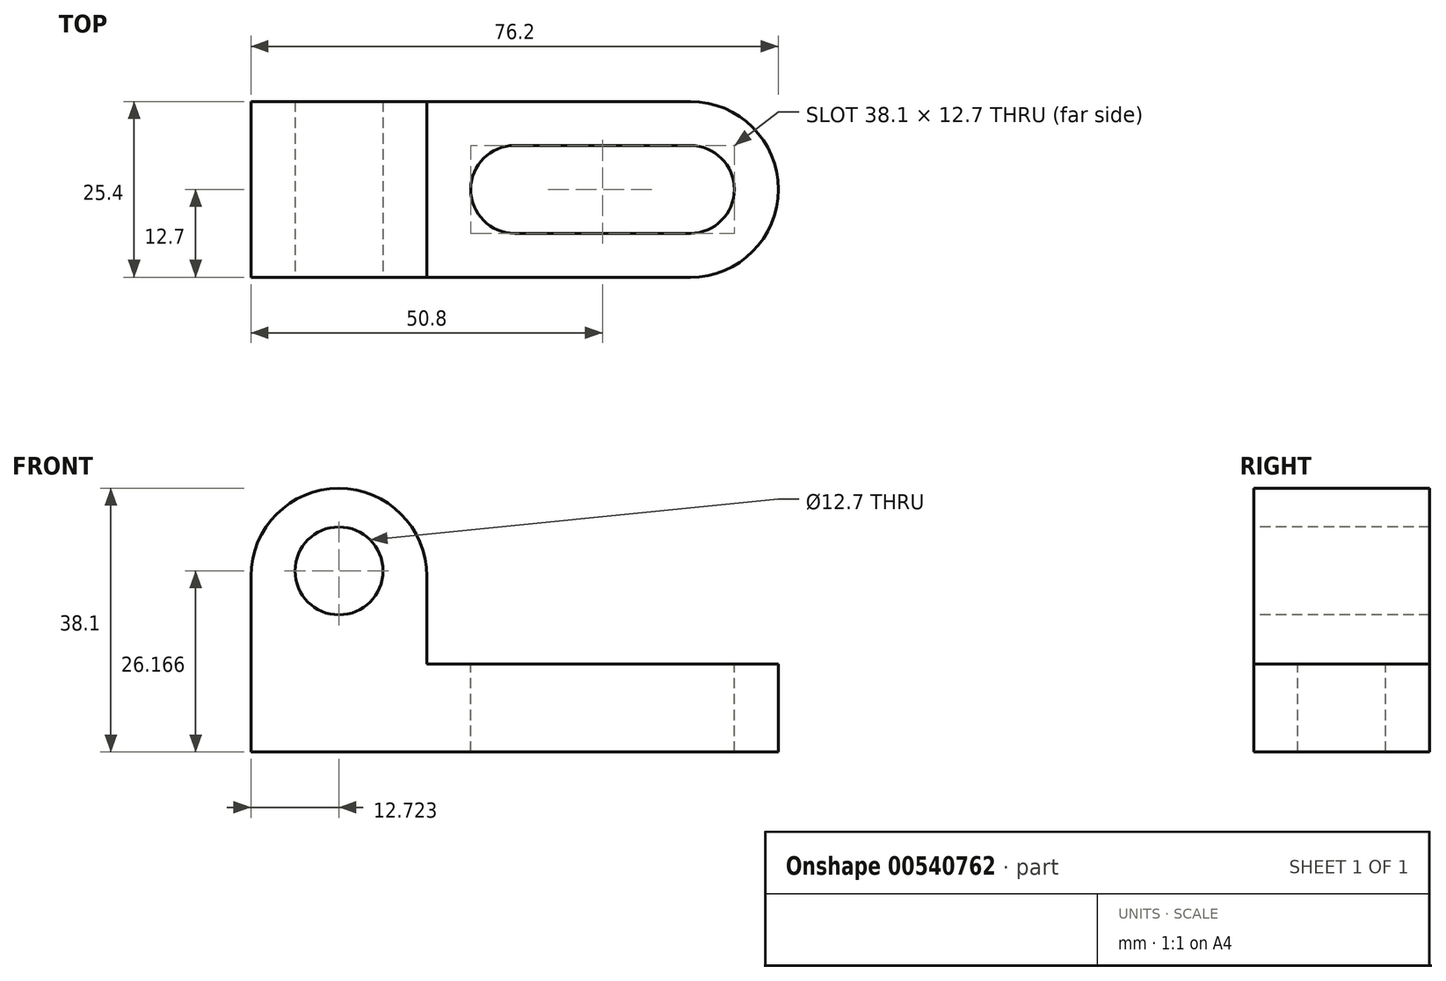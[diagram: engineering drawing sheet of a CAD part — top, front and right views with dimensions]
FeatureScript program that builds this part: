
annotation { "Feature Type Name" : "Feature", "Feature Type Description" : "" }
export const myFeature = defineFeature(function(context is Context, id is Id, definition is map)
    precondition{}
    {
        {
            var Q0;
            Q0=qCreatedBy(makeId("Front.planeOp"),FACE);
            var sketch = newSketch(context, id + "F0", { "sketchPlane" : qUnion([Q0])});
            skLineSegment(sketch, "E0", {"start": v(0, 0) * mm, "end": v(76.2, 0) * mm});
            skLineSegment(sketch, "E1", {"start": v(76.2, 0) * mm, "end": v(76.2, 12.7) * mm});
            skLineSegment(sketch, "E2", {"start": v(76.2, 12.7) * mm, "end": v(25.4, 12.7) * mm});
            skLineSegment(sketch, "E3", {"start": v(25.4, 12.7) * mm, "end": v(25.4, 38.1) * mm});
            skLineSegment(sketch, "E4", {"start": v(25.4, 38.1) * mm, "end": v(0, 38.1) * mm});
            skLineSegment(sketch, "E5", {"start": v(0, 38.1) * mm, "end": v(0, 0) * mm});
            skSolve(sketch);
        }
        {
            var Q0;
            Q0=makeQuery(id+"F0.imprint","IMPRINT",FACE,{"disambiguationData":[TD([[makeQuery(id+"F0.imprint","IMPRINT",EDGE,{"derivedFrom":sQuery(id+"F0.wireOp",EDGE,"E0")}),1.0]])]});
            extrude(context, id + "F1", {"entities" : qUnion([Q0]), "oppositeDirection" : true, "depth" : 25.4 * mm, "offsetDistance" : 25.4 * mm});
        }
        {
            var Q0;
            Q0=makeQuery(id+"F1.opExtrude","CAP_FACE",FACE,{"disambiguationData":[OSD([sQuery(id+"F0.wireOp",EDGE,"E0"),sQuery(id+"F0.wireOp",EDGE,"E1"),sQuery(id+"F0.wireOp",EDGE,"E2"),sQuery(id+"F0.wireOp",EDGE,"E3"),sQuery(id+"F0.wireOp",EDGE,"E4"),sQuery(id+"F0.wireOp",EDGE,"E5")])],"isStart":true});
            var sketch = newSketch(context, id + "F2", { "sketchPlane" : qUnion([Q0])});
            skCircle(sketch, "E6", {"center": v(12.72, 26.17) * mm, "radius": 6.35 * mm});
            skSolve(sketch);
        }
        {
            var Q0;
            Q0=makeQuery(id+"F2.imprint","IMPRINT",FACE,{"disambiguationData":[TD([[makeQuery(id+"F2.imprint","IMPRINT",EDGE,{"derivedFrom":sQuery(id+"F2.wireOp",EDGE,"E6")}),1.0]])]});
            extrude(context, id + "F3", {"entities" : qUnion([Q0]), "operationType" : NewBodyOperationType.REMOVE, "oppositeDirection" : true, "depth" : 52.07 * mm, "offsetDistance" : 25.4 * mm});
        }
        {
            var Q0;
            Q0=makeQuery(id+"F1.opExtrude","CAP_FACE",FACE,{"disambiguationData":[OSD([sQuery(id+"F0.wireOp",EDGE,"E0"),sQuery(id+"F0.wireOp",EDGE,"E1"),sQuery(id+"F0.wireOp",EDGE,"E2"),sQuery(id+"F0.wireOp",EDGE,"E3"),sQuery(id+"F0.wireOp",EDGE,"E4"),sQuery(id+"F0.wireOp",EDGE,"E5")])],"isStart":true});
            var sketch = newSketch(context, id + "F4", { "sketchPlane" : qUnion([Q0])});
            skArc(sketch, "E7", {"start": v(25.4, 25.4) * mm, "mid": v(12.7, 38.1) * mm, "end": v(0, 25.4) * mm});
            skPoint(sketch, "E7.endSnap0", {"position": v(25.4, 25.4) * mm});
            skSolve(sketch);
        }
        {
            var Q0;
            {var subQ0=sQuery(id+"F4.wireOp",EDGE,"E7");var subQ1=makeQuery(id+"F1.opExtrude","CAP_EDGE",EDGE,{"disambiguationData":[OSD([sQuery(id+"F0.wireOp",EDGE,"E3")])],"isStart":true});var subQ2=makeQuery(id+"F4.imprint","INTERSECT",VERTEX,{"derivedFrom":[subQ1,subQ0]});Q0=makeQuery(id+"F4.imprint","IMPRINT",FACE,{"disambiguationData":[TD([[makeQuery(id+"F4.imprint","IMPRINT",EDGE,{"disambiguationData":[TD([[subQ2,-1.0]])],"derivedFrom":subQ0}),-1.0]])]});}
            var Q1;
            {var subQ0=sQuery(id+"F4.wireOp",EDGE,"E7");var subQ1=makeQuery(id+"F1.opExtrude","CAP_EDGE",EDGE,{"disambiguationData":[OSD([sQuery(id+"F0.wireOp",EDGE,"E5")])],"isStart":true});var subQ2=makeQuery(id+"F4.imprint","INTERSECT",VERTEX,{"derivedFrom":[subQ1,subQ0]});Q1=makeQuery(id+"F4.imprint","IMPRINT",FACE,{"disambiguationData":[TD([[makeQuery(id+"F4.imprint","IMPRINT",EDGE,{"disambiguationData":[TD([[subQ2,1.0]])],"derivedFrom":subQ0}),-1.0]])]});}
            extrude(context, id + "F5", {"entities" : qUnion([Q0, Q1]), "operationType" : NewBodyOperationType.REMOVE, "oppositeDirection" : true, "depth" : 48.77 * mm, "offsetDistance" : 25.4 * mm});
        }
        {
            var Q0;
            Q0=makeQuery(id+"F1.opExtrude","SWEPT_FACE",FACE,{"disambiguationData":[OSD([sQuery(id+"F0.wireOp",EDGE,"E2")])]});
            var sketch = newSketch(context, id + "F6", { "sketchPlane" : qUnion([Q0])});
            skLineSegment(sketch, "E8", {"start": v(38.1, 19.05) * mm, "end": v(63.5, 19.05) * mm});
            skLineSegment(sketch, "E9", {"start": v(38.1, 6.35) * mm, "end": v(63.5, 6.35) * mm});
            skArc(sketch, "E10", {"start": v(38.1, 19.05) * mm, "mid": v(31.75, 12.7) * mm, "end": v(38.1, 6.35) * mm});
            skArc(sketch, "E11", {"start": v(63.5, 6.35) * mm, "mid": v(69.85, 12.7) * mm, "end": v(63.5, 19.05) * mm});
            skSolve(sketch);
        }
        {
            var Q0;
            Q0=makeQuery(id+"F6.imprint","IMPRINT",FACE,{"disambiguationData":[TD([[makeQuery(id+"F6.imprint","IMPRINT",EDGE,{"derivedFrom":sQuery(id+"F6.wireOp",EDGE,"E8")}),-1.0]])]});
            extrude(context, id + "F7", {"entities" : qUnion([Q0]), "operationType" : NewBodyOperationType.REMOVE, "oppositeDirection" : true, "depth" : 25.4 * mm, "offsetDistance" : 25.4 * mm});
        }
        {
            var Q0;
            Q0=makeQuery(id+"F1.opExtrude","SWEPT_FACE",FACE,{"disambiguationData":[OSD([sQuery(id+"F0.wireOp",EDGE,"E2")])]});
            var sketch = newSketch(context, id + "F8", { "sketchPlane" : qUnion([Q0])});
            skArc(sketch, "E12", {"start": v(63.5, 0) * mm, "mid": v(76.2, 12.7) * mm, "end": v(63.5, 25.4) * mm});
            skSolve(sketch);
        }
        {
            var Q0;
            {var subQ0=sQuery(id+"F8.wireOp",EDGE,"E12");var subQ1=sQuery(id+"F0.wireOp",EDGE,"E2");var subQ2=makeQuery(id+"F1.opExtrude","CAP_EDGE",EDGE,{"disambiguationData":[OSD([subQ1])],"isStart":false});var subQ3=makeQuery(id+"F8.imprint","INTERSECT",VERTEX,{"derivedFrom":[subQ2,subQ0]});Q0=makeQuery(id+"F8.imprint","IMPRINT",FACE,{"disambiguationData":[TD([[makeQuery(id+"F8.imprint","IMPRINT",EDGE,{"disambiguationData":[TD([[subQ3,1.0]])],"derivedFrom":subQ0}),-1.0]])]});}
            var Q1;
            {var subQ0=sQuery(id+"F8.wireOp",EDGE,"E12");var subQ1=sQuery(id+"F0.wireOp",EDGE,"E2");var subQ2=makeQuery(id+"F1.opExtrude","CAP_EDGE",EDGE,{"disambiguationData":[OSD([subQ1])],"isStart":true});var subQ3=makeQuery(id+"F8.imprint","INTERSECT",VERTEX,{"derivedFrom":[subQ2,subQ0]});Q1=makeQuery(id+"F8.imprint","IMPRINT",FACE,{"disambiguationData":[TD([[makeQuery(id+"F8.imprint","IMPRINT",EDGE,{"disambiguationData":[TD([[subQ3,-1.0]])],"derivedFrom":subQ0}),-1.0]])]});}
            extrude(context, id + "F9", {"entities" : qUnion([Q0, Q1]), "operationType" : NewBodyOperationType.REMOVE, "oppositeDirection" : true, "depth" : 25.4 * mm, "offsetDistance" : 25.4 * mm});
        }
    });
